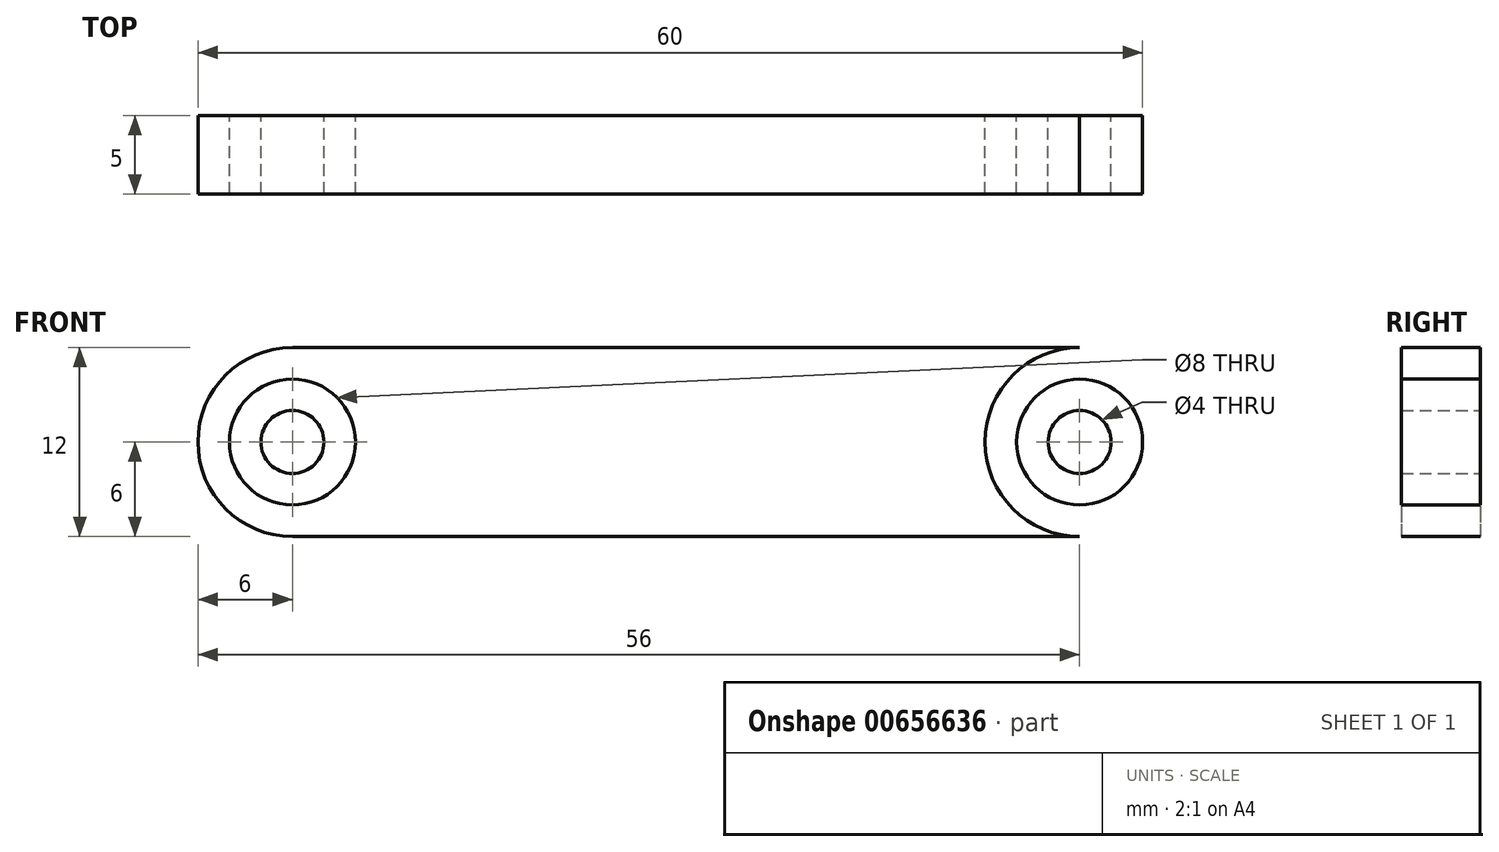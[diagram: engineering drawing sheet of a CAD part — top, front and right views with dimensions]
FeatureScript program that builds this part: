
annotation { "Feature Type Name" : "Feature", "Feature Type Description" : "" }
export const myFeature = defineFeature(function(context is Context, id is Id, definition is map)
    precondition{}
    {
        {
            var Q0;
            Q0=qCreatedBy(makeId("Front.planeOp"),FACE);
            var sketch = newSketch(context, id + "F0", { "sketchPlane" : qUnion([Q0])});
            skCircle(sketch, "E0", {"center": v(-25, 0) * mm, "radius": 2 * mm});
            skCircle(sketch, "E1", {"center": v(-25, 0) * mm, "radius": 4 * mm});
            skCircle(sketch, "E2", {"center": v(-25, 0) * mm, "radius": 6 * mm});
            skLineSegment(sketch, "E3", {"start": v(-25, 6) * mm, "end": v(0, 6) * mm});
            skLineSegment(sketch, "E4", {"start": v(-25, -6) * mm, "end": v(0, -6) * mm});
            skCircle(sketch, "E5.MirrorC", {"center": v(25, 0) * mm, "radius": 4 * mm});
            skCircle(sketch, "E6.MirrorC", {"center": v(25, 0) * mm, "radius": 6 * mm});
            skLineSegment(sketch, "E7.MirrorCS", {"start": v(25, 6) * mm, "end": v(0, 6) * mm});
            skLineSegment(sketch, "E8.MirrorCS", {"start": v(25, -6) * mm, "end": v(0, -6) * mm});
            skCircle(sketch, "E9.MirrorC", {"center": v(25, 0) * mm, "radius": 2 * mm});
            skSolve(sketch);
        }
        {
            var Q0;
            {var subQ1=sQuery(id+"F0.wireOp",EDGE,"E3");Q0=makeQuery(id+"F0.imprint","IMPRINT",FACE,{"disambiguationData":[TD([[makeQuery(id+"F0.imprint","IMPRINT",EDGE,{"derivedFrom":subQ1}),-1.0]])]});}
            var Q1;
            Q1=makeQuery(id+"F0.imprint","IMPRINT",FACE,{"disambiguationData":[TD([[makeQuery(id+"F0.imprint","IMPRINT",EDGE,{"derivedFrom":sQuery(id+"F0.wireOp",EDGE,"E1")}),-1.0]])]});
            var Q2;
            Q2=makeQuery(id+"F0.imprint","IMPRINT",FACE,{"disambiguationData":[TD([[makeQuery(id+"F0.imprint","IMPRINT",EDGE,{"derivedFrom":sQuery(id+"F0.wireOp",EDGE,"E0")}),1.0]])]});
            var Q3;
            Q3=makeQuery(id+"F0.imprint","IMPRINT",FACE,{"disambiguationData":[TD([[makeQuery(id+"F0.imprint","IMPRINT",EDGE,{"derivedFrom":sQuery(id+"F0.wireOp",EDGE,"E9.MirrorC")}),-1.0]])]});
            var Q4;
            Q4=makeQuery(id+"F0.imprint","IMPRINT",FACE,{"disambiguationData":[TD([[makeQuery(id+"F0.imprint","IMPRINT",EDGE,{"derivedFrom":sQuery(id+"F0.wireOp",EDGE,"E5.MirrorC")}),1.0]])]});
            extrude(context, id + "F1", {"entities" : qUnion([Q0, Q1, Q2, Q3, Q4]), "depth" : 5 * mm, "offsetDistance" : 25 * mm});
        }
    });
